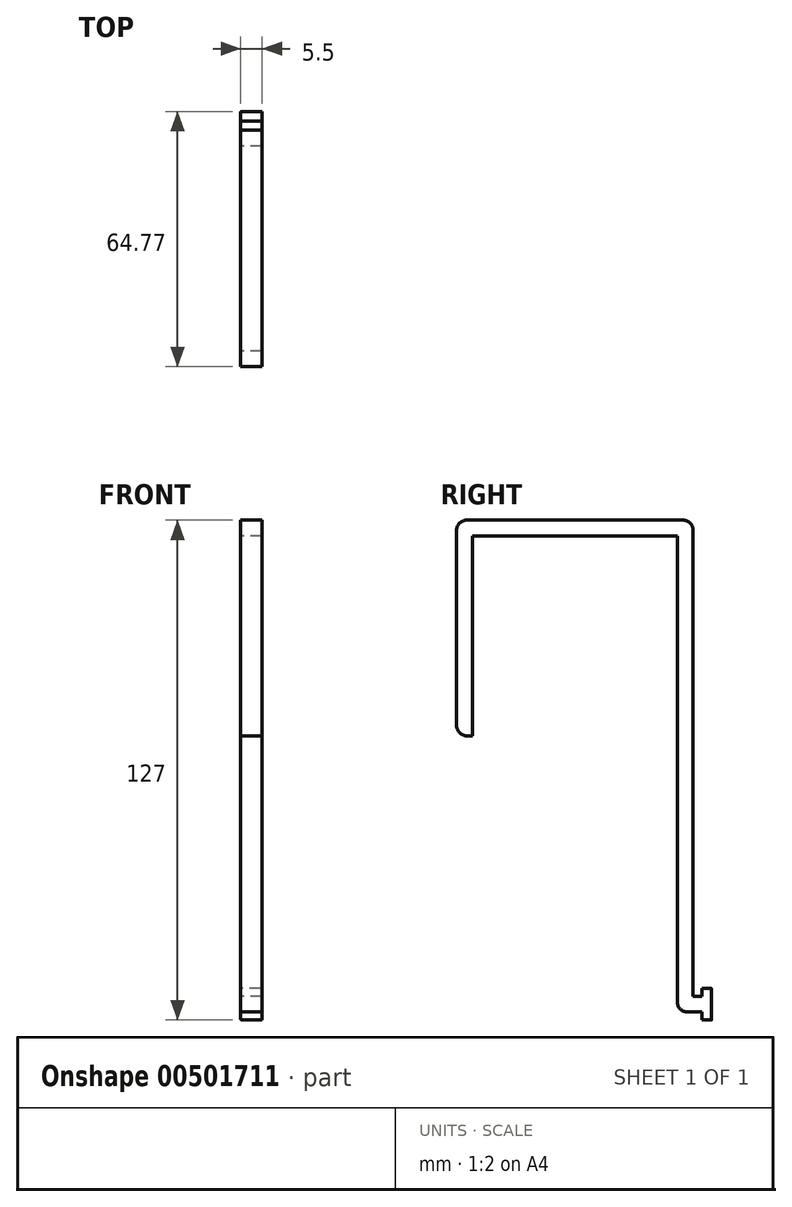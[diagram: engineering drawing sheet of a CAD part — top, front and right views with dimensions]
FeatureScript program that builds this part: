
annotation { "Feature Type Name" : "Feature", "Feature Type Description" : "" }
export const myFeature = defineFeature(function(context is Context, id is Id, definition is map)
    precondition{}
    {
        {
            var Q0;
            Q0=qCreatedBy(makeId("Right.planeOp"),FACE);
            var sketch = newSketch(context, id + "F0", { "sketchPlane" : qUnion([Q0])});
            skLineSegment(sketch, "E0", {"start": v(0, -29.4) * mm, "end": v(0, 0) * mm});
            skLineSegment(sketch, "E1", {"start": v(0, 0) * mm, "end": v(60.07, 0) * mm});
            skLineSegment(sketch, "E2", {"start": v(60.07, 0) * mm, "end": v(60.07, -121) * mm});
            skLineSegment(sketch, "E3", {"start": v(60.07, -121) * mm, "end": v(62.32, -121) * mm});
            skLineSegment(sketch, "E4", {"start": v(62.32, -121) * mm, "end": v(62.32, -119) * mm});
            skLineSegment(sketch, "E5", {"start": v(62.32, -119) * mm, "end": v(64.77, -119) * mm});
            skLineSegment(sketch, "E6", {"start": v(64.77, -119) * mm, "end": v(64.77, -127) * mm});
            skLineSegment(sketch, "E7", {"start": v(64.77, -127) * mm, "end": v(62.32, -127) * mm});
            skLineSegment(sketch, "E8", {"start": v(62.32, -127) * mm, "end": v(62.32, -125) * mm});
            skLineSegment(sketch, "E9", {"start": v(62.32, -125) * mm, "end": v(60.07, -125) * mm});
            skLineSegment(sketch, "E10", {"start": v(60.07, -125) * mm, "end": v(56.07, -125) * mm});
            skLineSegment(sketch, "E11", {"start": v(56.07, -125) * mm, "end": v(56.07, -4) * mm});
            skLineSegment(sketch, "E12", {"start": v(56.07, -4) * mm, "end": v(4, -4) * mm});
            skLineSegment(sketch, "E13", {"start": v(4, -4) * mm, "end": v(4, -54.8) * mm});
            skLineSegment(sketch, "E14", {"start": v(4, -54.8) * mm, "end": v(0, -54.8) * mm});
            skLineSegment(sketch, "E15", {"start": v(0, -54.8) * mm, "end": v(0, -29.4) * mm});
            skLineSegment(sketch, "E16", {"start": v(0, -29.4) * mm, "end": v(4, -29.4) * mm, "construction": true});
            skLineSegment(sketch, "E17", {"start": v(30.04, 0) * mm, "end": v(30.04, -4) * mm, "construction": true});
            skLineSegment(sketch, "E18", {"start": v(56.07, -29.4) * mm, "end": v(60.07, -29.4) * mm, "construction": true});
            skLineSegment(sketch, "E19", {"start": v(61.2, -121) * mm, "end": v(61.2, -125) * mm, "construction": true});
            skPoint(sketch, "E20", {"position": v(61.2, -123) * mm});
            skPoint(sketch, "E21", {"position": v(64.77, -123) * mm});
            skSolve(sketch);
        }
        {
            var Q0;
            Q0 = qSketchRegion(id + "F0", true);
            extrude(context, id + "F1", {"entities" : qUnion([Q0]), "depth" : 5.5 * mm, "offsetDistance" : 25.4 * mm});
        }
        {
            var Q0;
            Q0=makeQuery(id+"F1.opExtrude","CAP_EDGE",EDGE,{"disambiguationData":[OSD([sQuery(id+"F0.wireOp",EDGE,"E5")])],"isStart":false});
            var Q1;
            Q1=makeQuery(id+"F1.opExtrude","CAP_EDGE",EDGE,{"disambiguationData":[OSD([sQuery(id+"F0.wireOp",EDGE,"E7")])],"isStart":false});
            var Q2;
            Q2=makeQuery(id+"F1.opExtrude","CAP_EDGE",EDGE,{"disambiguationData":[OSD([sQuery(id+"F0.wireOp",EDGE,"E5")])],"isStart":true});
            var Q3;
            Q3=makeQuery(id+"F1.opExtrude","CAP_EDGE",EDGE,{"disambiguationData":[OSD([sQuery(id+"F0.wireOp",EDGE,"E7")])],"isStart":true});
            fillet(context, id + "F2", {"entities" : qUnion([Q0, Q1, Q2, Q3]), "radius" : 0.25 * mm, "tangentPropagation" : true, "allowEdgeOverflow" : false});
        }
        {
            var Q0;
            Q0=makeQuery(id+"F1.opExtrude","SWEPT_EDGE",EDGE,{"disambiguationData":[OSD([sQuery(id+"F0.wireOp",EDGE,"E1"),sQuery(id+"F0.wireOp",EDGE,"E2")])]});
            var Q1;
            Q1=makeQuery(id+"F1.opExtrude","SWEPT_EDGE",EDGE,{"disambiguationData":[OSD([sQuery(id+"F0.wireOp",EDGE,"E0"),sQuery(id+"F0.wireOp",EDGE,"E1")])]});
            var Q2;
            Q2=makeQuery(id+"F1.opExtrude","SWEPT_EDGE",EDGE,{"disambiguationData":[OSD([sQuery(id+"F0.wireOp",EDGE,"E10"),sQuery(id+"F0.wireOp",EDGE,"E11")])]});
            var Q3;
            Q3=makeQuery(id+"F1.opExtrude","SWEPT_EDGE",EDGE,{"disambiguationData":[OSD([sQuery(id+"F0.wireOp",EDGE,"E14"),sQuery(id+"F0.wireOp",EDGE,"E15")])]});
            fillet(context, id + "F3", {"entities" : qUnion([Q0, Q1, Q2, Q3]), "radius" : 2.54 * mm, "tangentPropagation" : true, "allowEdgeOverflow" : false});
        }
    });
